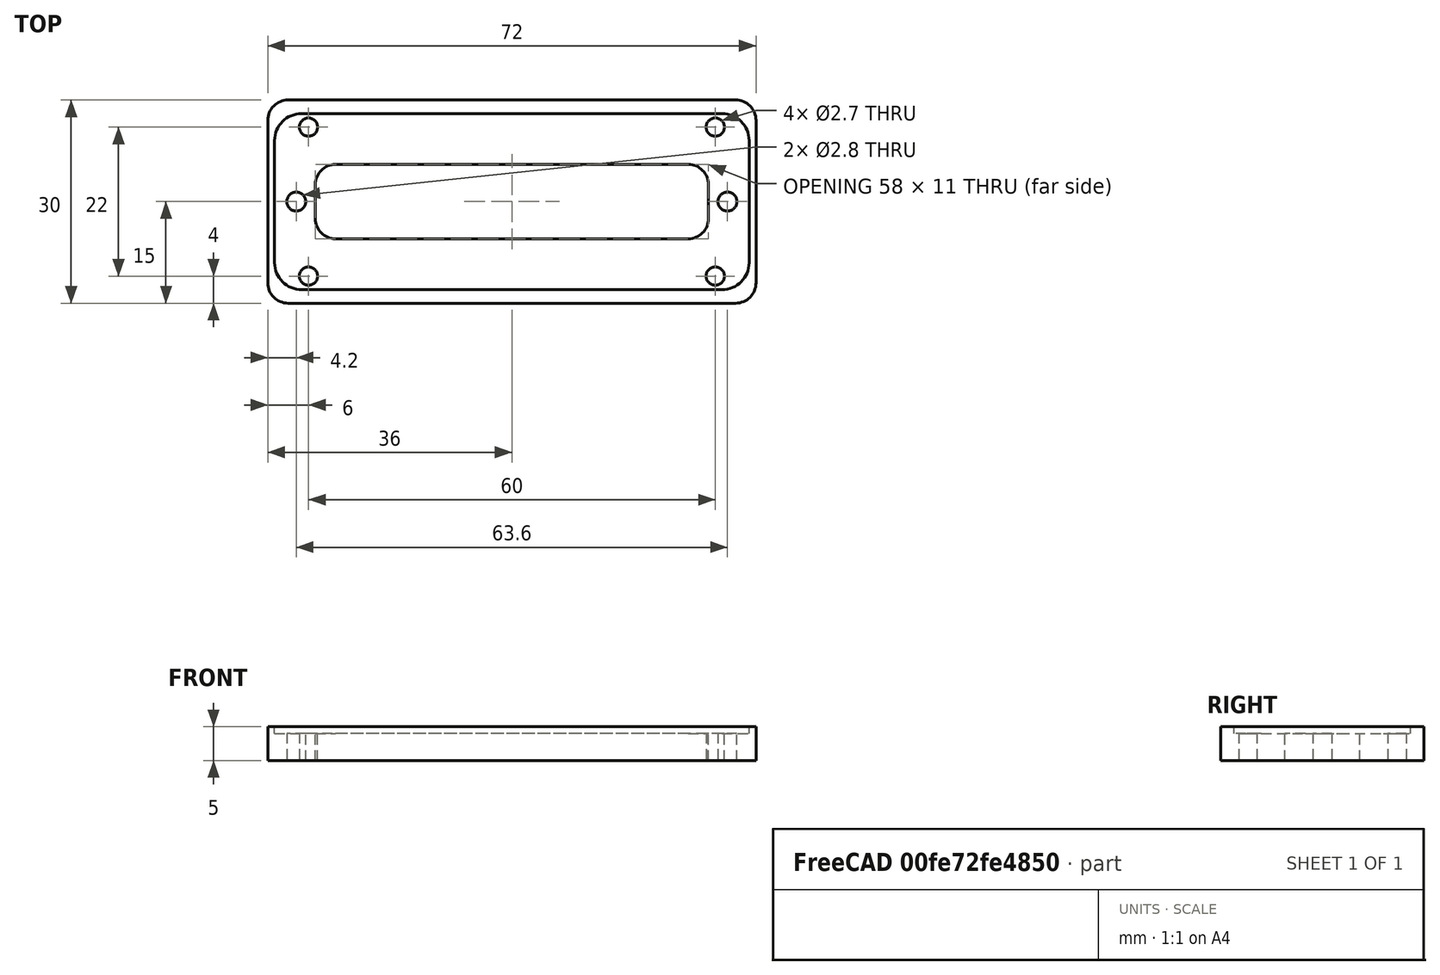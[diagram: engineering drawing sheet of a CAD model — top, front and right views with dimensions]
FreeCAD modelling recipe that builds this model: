
FCSTD DOCUMENT  (FreeCAD 0.19R)
Label: DBAdapter0
License: All rights reserved
LicenseURL: http://en.wikipedia.org/wiki/All_rights_reserved
objects: Sketcher::SketchObject×2, PartDesign::Pad×2, PartDesign::Fillet×2, PartDesign::Body×1, Mesh::Feature×1
note: 11 computed .brp shape members not serialized (recipe doc carries the construction recipe); baked Part::Feature solids carry a one-line shape summary decoded from their .brp

FEATURE [Sketcher::SketchObject] Sketch
  FullyConstrained = true
  MapMode = 5
  Support = -> [XY_Plane]
  sketch-geometry (14):
    g0: Circle CenterX=-30 CenterY=11 CenterZ=0 NormalX=0 NormalY=0 NormalZ=1 AngleXU=0 Radius=1.35
    g1: Circle CenterX=30 CenterY=11 CenterZ=0 NormalX=0 NormalY=0 NormalZ=1 AngleXU=0 Radius=1.35
    g2: Circle CenterX=-30 CenterY=-11 CenterZ=0 NormalX=0 NormalY=0 NormalZ=1 AngleXU=0 Radius=1.35
    g3: Circle CenterX=30 CenterY=-11 CenterZ=0 NormalX=0 NormalY=0 NormalZ=1 AngleXU=0 Radius=1.35
    g4: LineSegment StartX=-36 StartY=15 StartZ=0 EndX=36 EndY=15 EndZ=0
    g5: LineSegment StartX=36 StartY=15 StartZ=0 EndX=36 EndY=-15 EndZ=0
    g6: LineSegment StartX=36 StartY=-15 StartZ=0 EndX=-36 EndY=-15 EndZ=0
    g7: LineSegment StartX=-36 StartY=-15 StartZ=0 EndX=-36 EndY=15 EndZ=0
    g8: LineSegment StartX=-29 StartY=5.5 StartZ=0 EndX=29 EndY=5.5 EndZ=0
    g9: LineSegment StartX=29 StartY=5.5 StartZ=0 EndX=29 EndY=-5.5 EndZ=0
    g10: LineSegment StartX=29 StartY=-5.5 StartZ=0 EndX=-29 EndY=-5.5 EndZ=0
    g11: LineSegment StartX=-29 StartY=-5.5 StartZ=0 EndX=-29 EndY=5.5 EndZ=0
    g12: Circle CenterX=-31.8 CenterY=0 CenterZ=0 NormalX=0 NormalY=0 NormalZ=1 AngleXU=0 Radius=1.4
    g13: Circle CenterX=31.8 CenterY=0 CenterZ=0 NormalX=0 NormalY=0 NormalZ=1 AngleXU=0 Radius=1.4
  constraints (35):
    c: Symmetric(g3,g2,g-2)
    c: Symmetric(g3,g1,g-1)
    c: Symmetric(g1,g0,g-2)
    c: Distance(g0,g1) = 60
    c: Distance(g3,g1) = 22
    c: Diameter(g0) = 2.7
    c: Equal(g0,g1)
    c: Equal(g0,g2)
    c: Equal(g0,g3)
    c: Coincident(g4,g5)
    c: Coincident(g5,g6)
    c: Coincident(g6,g7)
    c: Coincident(g7,g4)
    c: Horizontal(g4)
    c: Horizontal(g6)
    c: Vertical(g5)
    c: Vertical(g7)
    c: Symmetric(g4,g6,g-1)
    c: Distance(g7) = 30
    c: Distance(g4) = 72
    c: Coincident(g8,g9)
    c: Coincident(g9,g10)
    c: Coincident(g10,g11)
    c: Coincident(g11,g8)
    c: Horizontal(g10)
    c: Vertical(g9)
    c: Symmetric(g10,g8,g-1)
    c: Symmetric(g8,g10,g-1)
    c: Distance(g11) = 11
    c: Distance(g8) = 58
    c: PointOnObject(g13,g-1)
    c: Diameter(g12) = 2.8
    c: Equal(g12,g13)
    c: Symmetric(g12,g13,g-1)
    c: Distance(g13,g12) = 63.6
FEATURE [PartDesign::Pad] Pad
  Direction = (1,1,1)
  Length = 4
  Length2 = 100
  Profile = -> Sketch
  Type = 0
FEATURE [Sketcher::SketchObject] Sketch001
  FullyConstrained = true
  MapMode = 5
  Placement = pos=(0,0,4) rot=(0,0,1;0rad)
  Support = -> [Pad]
  sketch-geometry (8):
    g0: LineSegment StartX=-35 StartY=13 StartZ=0 EndX=35 EndY=13 EndZ=0
    g1: LineSegment StartX=35 StartY=13 StartZ=0 EndX=35 EndY=-13 EndZ=0
    g2: LineSegment StartX=35 StartY=-13 StartZ=0 EndX=-35 EndY=-13 EndZ=0
    g3: LineSegment StartX=-35 StartY=-13 StartZ=0 EndX=-35 EndY=13 EndZ=0
    g4: LineSegment StartX=-36 StartY=15 StartZ=0 EndX=36 EndY=15 EndZ=0
    g5: LineSegment StartX=36 StartY=15 StartZ=0 EndX=36 EndY=-15 EndZ=0
    g6: LineSegment StartX=36 StartY=-15 StartZ=0 EndX=-36 EndY=-15 EndZ=0
    g7: LineSegment StartX=-36 StartY=-15 StartZ=0 EndX=-36 EndY=15 EndZ=0
  constraints (22):
    c: Coincident(g0,g1)
    c: Coincident(g1,g2)
    c: Coincident(g2,g3)
    c: Coincident(g3,g0)
    c: Horizontal(g0)
    c: Horizontal(g2)
    c: Vertical(g1)
    c: Vertical(g3)
    c: Coincident(g4,g5)
    c: Coincident(g5,g6)
    c: Coincident(g6,g7)
    c: Coincident(g7,g4)
    c: Horizontal(g4)
    c: Horizontal(g6)
    c: Vertical(g5)
    c: Vertical(g7)
    c: Symmetric(g0,g2,g-1)
    c: Distance(g0) = 70
    c: Distance(g1) = 26
    c: Symmetric(g4,g6,g-1)
    c: Distance(g4) = 72
    c: Distance(g5) = 30
FEATURE [PartDesign::Pad] Pad001
  BaseFeature = -> Pad
  Direction = (1,1,1)
  Length = 1
  Length2 = 100
  Profile = -> Sketch001
  Type = 0
FEATURE [PartDesign::Fillet] Fillet
  Base = -> Pad001 [Edge5,Edge1,Edge2,Edge8,Edge30,Edge33,Edge35,Edge31]
  BaseFeature = -> Pad001
  Radius = 3
  SupportTransform = false
FEATURE [PartDesign::Fillet] Fillet001
  Base = -> Fillet [Edge91,Edge93,Edge94,Edge92]
  BaseFeature = -> Fillet
  Radius = 4
  SupportTransform = false
FEATURE [PartDesign::Body] Body
  Group = -> [Sketch,Pad,Sketch001,Pad001,Fillet,Fillet001]
  Origin = -> Origin
  Tip = -> Fillet001
FEATURE [Mesh::Feature] Mesh  label="Fillet001 (Meshed)"
